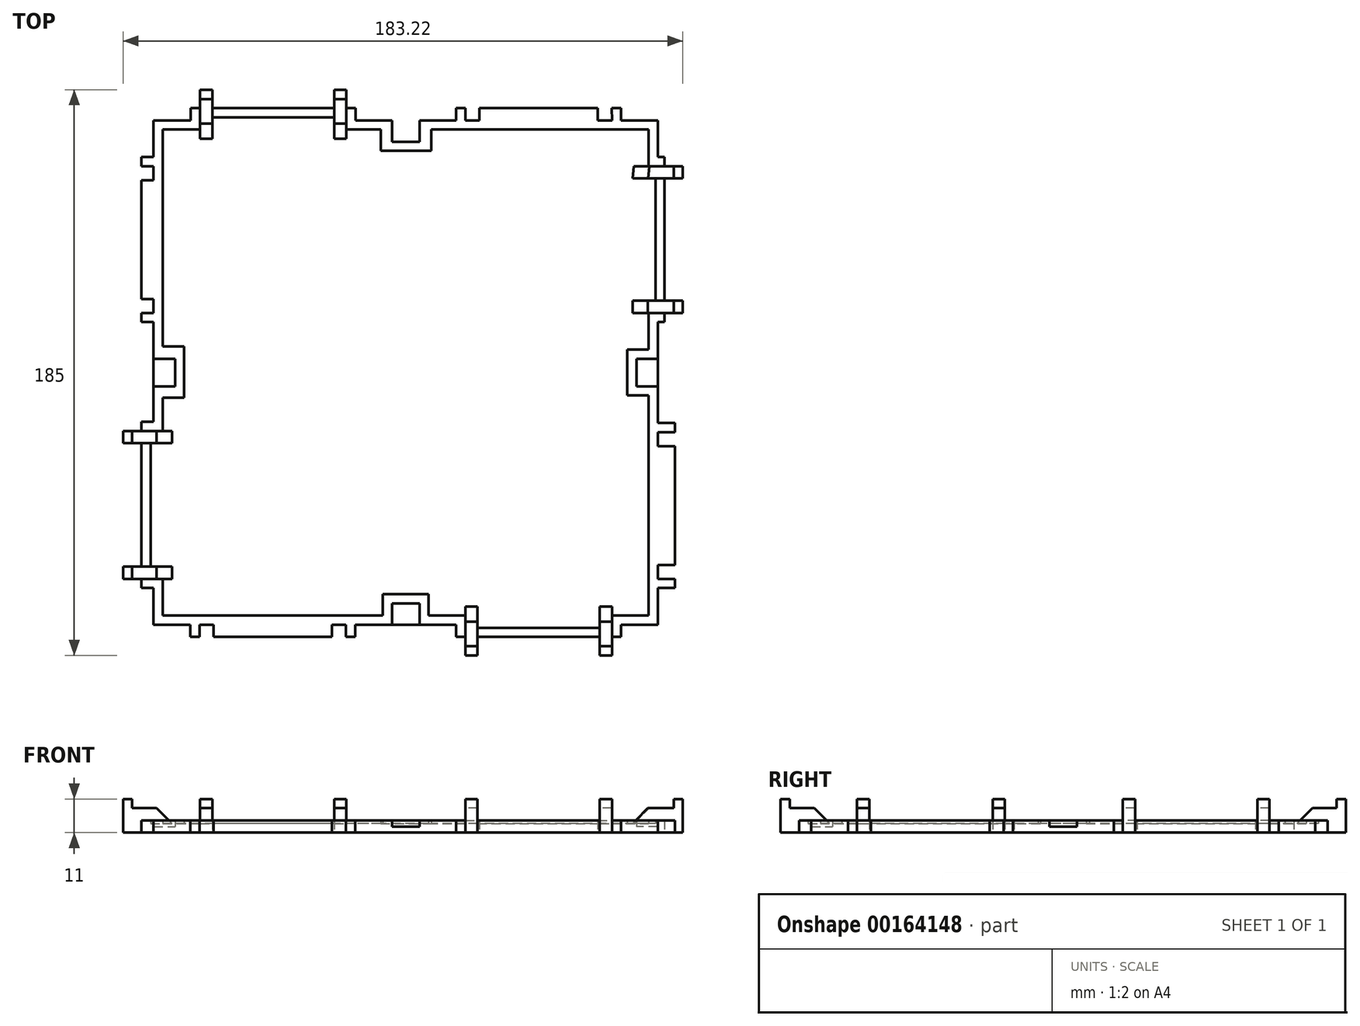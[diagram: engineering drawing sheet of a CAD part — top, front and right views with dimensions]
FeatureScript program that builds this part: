
annotation { "Feature Type Name" : "Feature", "Feature Type Description" : "" }
export const myFeature = defineFeature(function(context is Context, id is Id, definition is map)
    precondition{}
    {
        {
            var Q0;
            Q0=qCreatedBy(makeId("Top.planeOp"),FACE);
            var sketch = newSketch(context, id + "F0", { "sketchPlane" : qUnion([Q0])});
            skLineSegment(sketch, "E0.bottom", {"start": v(-87, 71.22) * mm, "end": v(-74.88, 71.22) * mm});
            skLineSegment(sketch, "E0.top", {"start": v(-87, -93.78) * mm, "end": v(-75, -93.78) * mm});
            skLineSegment(sketch, "E0.left", {"start": v(-87, 71.22) * mm, "end": v(-87, 59.22) * mm});
            skLineSegment(sketch, "E0.right", {"start": v(78, 71.22) * mm, "end": v(78, 59.22) * mm});
            skLineSegment(sketch, "E1", {"start": v(-87, 74.23) * mm, "end": v(-75, 74.23) * mm, "construction": true});
            skLineSegment(sketch, "E2.bottom", {"start": v(-74.88, 75.22) * mm, "end": v(-71.8, 75.22) * mm});
            skLineSegment(sketch, "E2.left", {"start": v(-74.88, 75.22) * mm, "end": v(-74.88, 71.22) * mm});
            skLineSegment(sketch, "E2.right", {"start": v(-20.88, 75.22) * mm, "end": v(-20.88, 71.22) * mm});
            skLineSegment(sketch, "E3", {"start": v(-74.8, 76.18) * mm, "end": v(-71.8, 76.18) * mm, "construction": true});
            skLineSegment(sketch, "E4.bottom", {"start": v(-71.8, 81.22) * mm, "end": v(-67.8, 81.22) * mm});
            skLineSegment(sketch, "E4.left", {"start": v(-71.8, 81.22) * mm, "end": v(-71.8, 75.22) * mm});
            skLineSegment(sketch, "E4.right", {"start": v(-67.8, 81.22) * mm, "end": v(-67.8, 75.22) * mm});
            skLineSegment(sketch, "E5", {"start": v(-20.88, 76.3) * mm, "end": v(-23.88, 76.3) * mm, "construction": true});
            skLineSegment(sketch, "E6.bottom", {"start": v(-27.88, 81.22) * mm, "end": v(-23.88, 81.22) * mm});
            skLineSegment(sketch, "E6.left", {"start": v(-27.88, 81.22) * mm, "end": v(-27.88, 75.22) * mm});
            skLineSegment(sketch, "E6.right", {"start": v(-23.88, 81.22) * mm, "end": v(-23.88, 75.22) * mm});
            skLineSegment(sketch, "E7.bottom", {"start": v(12, 75.22) * mm, "end": v(15, 75.22) * mm});
            skLineSegment(sketch, "E7.top", {"start": v(15, 71.22) * mm, "end": v(19.6, 71.22) * mm});
            skLineSegment(sketch, "E7.left", {"start": v(12, 75.22) * mm, "end": v(12, 71.22) * mm});
            skLineSegment(sketch, "E7.right", {"start": v(66, 75.22) * mm, "end": v(66, 71.22) * mm});
            skLineSegment(sketch, "E8", {"start": v(66, 73.22) * mm, "end": v(63, 73.22) * mm, "construction": true});
            skLineSegment(sketch, "E9", {"start": v(63, 73.22) * mm, "end": v(63, 73.22) * mm, "construction": true});
            skLineSegment(sketch, "E10", {"start": v(15, 75.22) * mm, "end": v(15, 71.22) * mm});
            skLineSegment(sketch, "E11", {"start": v(19.6, 75.22) * mm, "end": v(19.6, 71.22) * mm});
            skLineSegment(sketch, "E12", {"start": v(62.99, 75.22) * mm, "end": v(63, 71.22) * mm});
            skLineSegment(sketch, "E13", {"start": v(58.39, 75.22) * mm, "end": v(58.4, 71.22) * mm});
            skLineSegment(sketch, "E14.bottom", {"start": v(78, 59.22) * mm, "end": v(80.22, 59.22) * mm});
            skLineSegment(sketch, "E14.top", {"start": v(78, 5.22) * mm, "end": v(80.22, 5.22) * mm});
            skLineSegment(sketch, "E14.right", {"start": v(80.22, 59.22) * mm, "end": v(80.22, 56.22) * mm});
            skLineSegment(sketch, "E15.bottom", {"start": v(80.22, 56.22) * mm, "end": v(86.22, 56.22) * mm});
            skLineSegment(sketch, "E15.top", {"start": v(80.22, 52.22) * mm, "end": v(86.22, 52.22) * mm});
            skLineSegment(sketch, "E15.right", {"start": v(86.22, 56.22) * mm, "end": v(86.22, 52.22) * mm});
            skLineSegment(sketch, "E16.bottom", {"start": v(80.22, 12.22) * mm, "end": v(86.22, 12.22) * mm});
            skLineSegment(sketch, "E16.top", {"start": v(80.22, 8.22) * mm, "end": v(86.22, 8.22) * mm});
            skLineSegment(sketch, "E16.right", {"start": v(86.22, 12.22) * mm, "end": v(86.22, 8.22) * mm});
            skLineSegment(sketch, "E17.bottom", {"start": v(78, -27.78) * mm, "end": v(83.62, -27.78) * mm});
            skLineSegment(sketch, "E17.top", {"start": v(78, -81.78) * mm, "end": v(83.62, -81.78) * mm});
            skLineSegment(sketch, "E17.left", {"start": v(78, -30.78) * mm, "end": v(78, -35.38) * mm});
            skLineSegment(sketch, "E17.right", {"start": v(83.62, -27.78) * mm, "end": v(83.62, -30.78) * mm});
            skLineSegment(sketch, "E18.trimOffspring", {"start": v(19.6, 75.22) * mm, "end": v(58.39, 75.22) * mm});
            skLineSegment(sketch, "E19.trimOffspring", {"start": v(62.99, 75.22) * mm, "end": v(66, 75.22) * mm});
            skLineSegment(sketch, "E20", {"start": v(83.62, -78.78) * mm, "end": v(78, -78.78) * mm});
            skLineSegment(sketch, "E21", {"start": v(83.62, -74.18) * mm, "end": v(78, -74.18) * mm});
            skLineSegment(sketch, "E22", {"start": v(83.62, -30.78) * mm, "end": v(78, -30.78) * mm});
            skLineSegment(sketch, "E23", {"start": v(83.62, -35.38) * mm, "end": v(78, -35.38) * mm});
            skLineSegment(sketch, "E24.trimOffspring", {"start": v(83.62, -35.38) * mm, "end": v(83.62, -74.18) * mm});
            skLineSegment(sketch, "E25.trimOffspring", {"start": v(83.62, -78.78) * mm, "end": v(83.62, -81.78) * mm});
            skLineSegment(sketch, "E26.bottom", {"start": v(66, -97.78) * mm, "end": v(63, -97.78) * mm});
            skLineSegment(sketch, "E26.left", {"start": v(66, -97.78) * mm, "end": v(66, -93.78) * mm});
            skLineSegment(sketch, "E26.right", {"start": v(12, -97.78) * mm, "end": v(12, -93.78) * mm});
            skLineSegment(sketch, "E27.top", {"start": v(59, -103.78) * mm, "end": v(63, -103.78) * mm});
            skLineSegment(sketch, "E27.left", {"start": v(59, -97.78) * mm, "end": v(59, -103.78) * mm});
            skLineSegment(sketch, "E27.right", {"start": v(63, -97.78) * mm, "end": v(63, -103.78) * mm});
            skLineSegment(sketch, "E28.top", {"start": v(15, -103.78) * mm, "end": v(19, -103.78) * mm});
            skLineSegment(sketch, "E28.left", {"start": v(15, -97.4) * mm, "end": v(15, -103.78) * mm});
            skLineSegment(sketch, "E28.right", {"start": v(19, -97.78) * mm, "end": v(19, -103.78) * mm});
            skLineSegment(sketch, "E29.trimOffspring", {"start": v(58.4, 73.23) * mm, "end": v(58.39, 73.23) * mm, "construction": true});
            skLineSegment(sketch, "E30.bottom", {"start": v(-72, -93.78) * mm, "end": v(-67.4, -93.78) * mm});
            skLineSegment(sketch, "E30.top", {"start": v(-75, -97.78) * mm, "end": v(-72, -97.78) * mm});
            skLineSegment(sketch, "E30.left", {"start": v(-75, -93.78) * mm, "end": v(-75, -97.78) * mm});
            skLineSegment(sketch, "E30.right", {"start": v(-21, -93.78) * mm, "end": v(-21, -97.78) * mm});
            skLineSegment(sketch, "E31", {"start": v(-72, -97.78) * mm, "end": v(-72, -93.78) * mm});
            skLineSegment(sketch, "E32", {"start": v(-67.4, -97.78) * mm, "end": v(-67.4, -93.78) * mm});
            skLineSegment(sketch, "E33", {"start": v(-24, -93.78) * mm, "end": v(-24, -97.78) * mm});
            skLineSegment(sketch, "E34", {"start": v(-28.6, -93.78) * mm, "end": v(-28.6, -97.78) * mm});
            skLineSegment(sketch, "E35.trimOffspring", {"start": v(-67.4, -97.78) * mm, "end": v(-28.6, -97.78) * mm});
            skLineSegment(sketch, "E36.trimOffspring", {"start": v(-24, -97.78) * mm, "end": v(-21, -97.78) * mm});
            skLineSegment(sketch, "E37.bottom", {"start": v(-91, -27.4) * mm, "end": v(-87, -27.4) * mm});
            skLineSegment(sketch, "E37.top", {"start": v(-91, -81.78) * mm, "end": v(-87, -81.78) * mm});
            skLineSegment(sketch, "E37.left", {"start": v(-91, -27.4) * mm, "end": v(-91, -30.4) * mm});
            skLineSegment(sketch, "E38.bottom", {"start": v(-97, -74.78) * mm, "end": v(-91.24, -74.78) * mm});
            skLineSegment(sketch, "E38.top", {"start": v(-97, -78.78) * mm, "end": v(-91, -78.78) * mm});
            skLineSegment(sketch, "E38.left", {"start": v(-97, -74.78) * mm, "end": v(-97, -78.78) * mm});
            skLineSegment(sketch, "E39.bottom", {"start": v(-97, -30.4) * mm, "end": v(-91, -30.4) * mm});
            skLineSegment(sketch, "E39.top", {"start": v(-97, -34.4) * mm, "end": v(-91, -34.4) * mm});
            skLineSegment(sketch, "E39.left", {"start": v(-97, -30.4) * mm, "end": v(-97, -34.4) * mm});
            skLineSegment(sketch, "E40.bottom", {"start": v(-91, 59.22) * mm, "end": v(-87, 59.22) * mm});
            skLineSegment(sketch, "E40.top", {"start": v(-91, 5.22) * mm, "end": v(-87, 5.22) * mm});
            skLineSegment(sketch, "E40.left", {"start": v(-91, 59.22) * mm, "end": v(-91, 56.22) * mm});
            skLineSegment(sketch, "E40.right", {"start": v(-87, 56.22) * mm, "end": v(-87, 51.62) * mm});
            skLineSegment(sketch, "E41", {"start": v(-91, 56.22) * mm, "end": v(-87, 56.22) * mm});
            skLineSegment(sketch, "E42", {"start": v(-91, 51.62) * mm, "end": v(-87, 51.62) * mm});
            skLineSegment(sketch, "E43", {"start": v(-91, 8.22) * mm, "end": v(-87, 8.22) * mm});
            skLineSegment(sketch, "E44", {"start": v(-91, 12.82) * mm, "end": v(-87, 12.82) * mm});
            skLineSegment(sketch, "E45.trimOffspring", {"start": v(-91, 51.62) * mm, "end": v(-91, 12.82) * mm});
            skLineSegment(sketch, "E46.trimOffspring", {"start": v(-91, 8.22) * mm, "end": v(-91, 5.22) * mm});
            skLineSegment(sketch, "E47", {"start": v(-67.8, 78.22) * mm, "end": v(-71.8, 78.22) * mm});
            skLineSegment(sketch, "E48", {"start": v(-27.88, 78.22) * mm, "end": v(-23.88, 78.22) * mm});
            skLineSegment(sketch, "E49", {"start": v(83.22, 56.22) * mm, "end": v(83.22, 52.22) * mm});
            skLineSegment(sketch, "E50", {"start": v(83.22, 12.22) * mm, "end": v(83.22, 8.22) * mm});
            skLineSegment(sketch, "E51", {"start": v(15, -100.78) * mm, "end": v(19, -100.78) * mm});
            skLineSegment(sketch, "E52", {"start": v(63, -100.78) * mm, "end": v(59, -100.78) * mm});
            skLineSegment(sketch, "E53", {"start": v(-94, -78.78) * mm, "end": v(-94, -74.78) * mm});
            skLineSegment(sketch, "E54", {"start": v(-94, -30.4) * mm, "end": v(-94, -34.4) * mm});
            skLineSegment(sketch, "E55.bottom", {"start": v(-91, -78.78) * mm, "end": v(-81, -78.78) * mm});
            skLineSegment(sketch, "E55.top", {"start": v(-91, -74.78) * mm, "end": v(-81, -74.78) * mm});
            skLineSegment(sketch, "E55.right", {"start": v(-81, -78.78) * mm, "end": v(-81, -74.78) * mm});
            skLineSegment(sketch, "E56.trimOffspring", {"start": v(-87, -81.78) * mm, "end": v(-87, -93.78) * mm});
            skLineSegment(sketch, "E57.bottom", {"start": v(-91, -30.4) * mm, "end": v(-81, -30.4) * mm});
            skLineSegment(sketch, "E57.top", {"start": v(-91, -34.4) * mm, "end": v(-81, -34.4) * mm});
            skLineSegment(sketch, "E57.right", {"start": v(-81, -30.4) * mm, "end": v(-81, -34.4) * mm});
            skLineSegment(sketch, "E58.trimOffspring", {"start": v(66, -93.78) * mm, "end": v(78, -93.78) * mm});
            skLineSegment(sketch, "E59.top", {"start": v(19, -87.78) * mm, "end": v(15, -87.78) * mm});
            skLineSegment(sketch, "E59.left", {"start": v(19, -97.78) * mm, "end": v(19, -87.78) * mm});
            skLineSegment(sketch, "E59.right", {"start": v(15, -97.78) * mm, "end": v(15, -87.78) * mm});
            skLineSegment(sketch, "E60.top", {"start": v(59, -87.78) * mm, "end": v(63, -87.78) * mm});
            skLineSegment(sketch, "E60.left", {"start": v(59, -97.78) * mm, "end": v(59, -87.78) * mm});
            skLineSegment(sketch, "E60.right", {"start": v(63, -97.78) * mm, "end": v(63, -87.78) * mm});
            skLineSegment(sketch, "E61.trimOffspring", {"start": v(59, -97.78) * mm, "end": v(19, -97.78) * mm});
            skLineSegment(sketch, "E62.trimOffspring", {"start": v(15, -97.78) * mm, "end": v(12, -97.78) * mm});
            skLineSegment(sketch, "E63.trimOffspring", {"start": v(-91, -34.4) * mm, "end": v(-91, -74.78) * mm});
            skLineSegment(sketch, "E64.trimOffspring", {"start": v(-91, -78.78) * mm, "end": v(-91, -81.78) * mm});
            skLineSegment(sketch, "E65.trimOffspring", {"start": v(78, 5.22) * mm, "end": v(78, -27.78) * mm});
            skLineSegment(sketch, "E66.bottom", {"start": v(80.22, 56.22) * mm, "end": v(70.22, 56.22) * mm});
            skLineSegment(sketch, "E66.top", {"start": v(80.22, 52.22) * mm, "end": v(69.78, 52.22) * mm});
            skLineSegment(sketch, "E66.right", {"start": v(70.22, 56.22) * mm, "end": v(69.78, 52.22) * mm});
            skLineSegment(sketch, "E67.bottom", {"start": v(80.22, 12.22) * mm, "end": v(69.78, 12.22) * mm});
            skLineSegment(sketch, "E67.top", {"start": v(79.78, 8.22) * mm, "end": v(69.78, 8.22) * mm});
            skLineSegment(sketch, "E67.right", {"start": v(69.78, 12.22) * mm, "end": v(69.78, 8.22) * mm});
            skLineSegment(sketch, "E68.trimOffspring", {"start": v(80.22, 8.22) * mm, "end": v(80.22, 5.22) * mm});
            skLineSegment(sketch, "E69.trimOffspring", {"start": v(80.22, 52.22) * mm, "end": v(80.22, 12.22) * mm});
            skLineSegment(sketch, "E70.trimOffspring", {"start": v(-20.88, 71.22) * mm, "end": v(12, 71.22) * mm});
            skLineSegment(sketch, "E71.top", {"start": v(-71.8, 65.22) * mm, "end": v(-67.8, 65.22) * mm});
            skLineSegment(sketch, "E71.left", {"start": v(-71.8, 75.22) * mm, "end": v(-71.8, 65.22) * mm});
            skLineSegment(sketch, "E71.right", {"start": v(-67.8, 75.22) * mm, "end": v(-67.8, 65.22) * mm});
            skLineSegment(sketch, "E72.top", {"start": v(-27.88, 65.22) * mm, "end": v(-23.88, 65.22) * mm});
            skLineSegment(sketch, "E72.left", {"start": v(-27.88, 75.22) * mm, "end": v(-27.88, 65.22) * mm});
            skLineSegment(sketch, "E72.right", {"start": v(-23.88, 75.22) * mm, "end": v(-23.88, 65.22) * mm});
            skLineSegment(sketch, "E73.trimOffspring", {"start": v(-23.88, 75.22) * mm, "end": v(-20.88, 75.22) * mm});
            skLineSegment(sketch, "E74.trimOffspring", {"start": v(-67.8, 75.22) * mm, "end": v(-27.88, 75.22) * mm});
            skLineSegment(sketch, "E75.bottom", {"start": v(-9, 71.22) * mm, "end": v(0, 71.22) * mm});
            skLineSegment(sketch, "E75.top", {"start": v(-9, 64.22) * mm, "end": v(0, 64.22) * mm});
            skLineSegment(sketch, "E75.left", {"start": v(-9, 71.22) * mm, "end": v(-9, 64.22) * mm});
            skLineSegment(sketch, "E75.right", {"start": v(0, 71.22) * mm, "end": v(0, 64.22) * mm});
            skLineSegment(sketch, "E76.bottom", {"start": v(78, -6.78) * mm, "end": v(71, -6.78) * mm});
            skLineSegment(sketch, "E76.top", {"start": v(78, -15.78) * mm, "end": v(71, -15.78) * mm});
            skLineSegment(sketch, "E76.left", {"start": v(78, -6.78) * mm, "end": v(78, -15.78) * mm});
            skLineSegment(sketch, "E76.right", {"start": v(71, -6.78) * mm, "end": v(71, -15.78) * mm});
            skLineSegment(sketch, "E77.bottom", {"start": v(-9, -93.78) * mm, "end": v(0, -93.78) * mm});
            skLineSegment(sketch, "E77.top", {"start": v(-9, -86.78) * mm, "end": v(0, -86.78) * mm});
            skLineSegment(sketch, "E77.left", {"start": v(-9, -93.78) * mm, "end": v(-9, -86.78) * mm});
            skLineSegment(sketch, "E77.right", {"start": v(0, -93.78) * mm, "end": v(0, -86.78) * mm});
            skLineSegment(sketch, "E78.bottom", {"start": v(-87, -6.78) * mm, "end": v(-80, -6.78) * mm});
            skLineSegment(sketch, "E78.top", {"start": v(-87, -15.78) * mm, "end": v(-80, -15.78) * mm});
            skLineSegment(sketch, "E78.left", {"start": v(-87, -6.78) * mm, "end": v(-87, -15.78) * mm});
            skLineSegment(sketch, "E78.right", {"start": v(-80, -6.78) * mm, "end": v(-80, -15.78) * mm});
            skLineSegment(sketch, "E79", {"start": v(-84, 71.22) * mm, "end": v(-84, 68.22) * mm, "construction": true});
            skLineSegment(sketch, "E80", {"start": v(75, 71.22) * mm, "end": v(75, 68.22) * mm, "construction": true});
            skLineSegment(sketch, "E81", {"start": v(75, -93.78) * mm, "end": v(75, -90.78) * mm, "construction": true});
            skLineSegment(sketch, "E82", {"start": v(-84, -93.78) * mm, "end": v(-84, -90.78) * mm, "construction": true});
            skLineSegment(sketch, "E83", {"start": v(0, -86.78) * mm, "end": v(3, -86.78) * mm, "construction": true});
            skLineSegment(sketch, "E84", {"start": v(0, -83.78) * mm, "end": v(0, -86.78) * mm, "construction": true});
            skLineSegment(sketch, "E85", {"start": v(-9, -86.78) * mm, "end": v(-12, -86.78) * mm, "construction": true});
            skLineSegment(sketch, "E86", {"start": v(-9, -83.78) * mm, "end": v(-9, -86.78) * mm, "construction": true});
            skLineSegment(sketch, "E87", {"start": v(-9, 64.22) * mm, "end": v(-9, 61.22) * mm, "construction": true});
            skLineSegment(sketch, "E88", {"start": v(71, -15.78) * mm, "end": v(71, -18.78) * mm, "construction": true});
            skLineSegment(sketch, "E89", {"start": v(71, -6.78) * mm, "end": v(71, -3.78) * mm, "construction": true});
            skLineSegment(sketch, "E90", {"start": v(71, -6.78) * mm, "end": v(68, -6.78) * mm, "construction": true});
            skLineSegment(sketch, "E91", {"start": v(-80, -6.78) * mm, "end": v(-77, -6.78) * mm, "construction": true});
            skLineSegment(sketch, "E92", {"start": v(-84, 68.22) * mm, "end": v(75, 68.22) * mm, "construction": true});
            skLineSegment(sketch, "E93", {"start": v(75, -90.78) * mm, "end": v(-84, -90.78) * mm, "construction": true});
            skLineSegment(sketch, "E94", {"start": v(-84, -90.78) * mm, "end": v(-84, 68.22) * mm, "construction": true});
            skLineSegment(sketch, "E95", {"start": v(6.55, -83.78) * mm, "end": v(-16.3, -83.78) * mm});
            skLineSegment(sketch, "E96", {"start": v(-12, -90.78) * mm, "end": v(-12, -83.78) * mm});
            skLineSegment(sketch, "E97", {"start": v(3, -90.78) * mm, "end": v(3, -83.78) * mm});
            skLineSegment(sketch, "E98", {"start": v(-12.66, 61.22) * mm, "end": v(3.83, 61.22) * mm});
            skLineSegment(sketch, "E99", {"start": v(-12.66, 61.22) * mm, "end": v(-12.66, 68.22) * mm});
            skLineSegment(sketch, "E100", {"start": v(3.83, 61.22) * mm, "end": v(3.83, 68.22) * mm});
            skLineSegment(sketch, "E101", {"start": v(75, -18.78) * mm, "end": v(68.64, -18.78) * mm});
            skLineSegment(sketch, "E102", {"start": v(75, -3.78) * mm, "end": v(68, -3.78) * mm});
            skLineSegment(sketch, "E103", {"start": v(68, -3.78) * mm, "end": v(68, -18.78) * mm});
            skLineSegment(sketch, "E104", {"start": v(68.64, -18.78) * mm, "end": v(68, -18.78) * mm});
            skLineSegment(sketch, "E105", {"start": v(-77, -2.75) * mm, "end": v(-77, -19.51) * mm});
            skLineSegment(sketch, "E106", {"start": v(-77, -19.51) * mm, "end": v(-84, -19.51) * mm});
            skLineSegment(sketch, "E107", {"start": v(-77, -2.75) * mm, "end": v(-84, -2.75) * mm});
            skLineSegment(sketch, "E108", {"start": v(-84, 68.22) * mm, "end": v(-84, -2.75) * mm});
            skLineSegment(sketch, "E109", {"start": v(-84, -19.51) * mm, "end": v(-84, -30.4) * mm});
            skLineSegment(sketch, "E110", {"start": v(-12, -90.78) * mm, "end": v(-84, -90.78) * mm});
            skLineSegment(sketch, "E111", {"start": v(-84, -78.78) * mm, "end": v(-84, -90.78) * mm});
            skLineSegment(sketch, "E112", {"start": v(3, -90.78) * mm, "end": v(15, -90.78) * mm});
            skLineSegment(sketch, "E113", {"start": v(63, -90.78) * mm, "end": v(75, -90.78) * mm});
            skLineSegment(sketch, "E114", {"start": v(75, -90.78) * mm, "end": v(75, -18.78) * mm});
            skLineSegment(sketch, "E115", {"start": v(75, -3.78) * mm, "end": v(75, 8.22) * mm});
            skLineSegment(sketch, "E116", {"start": v(75, 56.22) * mm, "end": v(75, 68.22) * mm});
            skLineSegment(sketch, "E117", {"start": v(75, 68.22) * mm, "end": v(3.83, 68.22) * mm});
            skLineSegment(sketch, "E118", {"start": v(-12.66, 68.22) * mm, "end": v(-23.88, 68.22) * mm});
            skLineSegment(sketch, "E119.trimOffspring", {"start": v(75, 8.22) * mm, "end": v(75, -90.78) * mm, "construction": true});
            skLineSegment(sketch, "E120", {"start": v(-88, -34.4) * mm, "end": v(-88, -74.78) * mm});
            skLineSegment(sketch, "E121", {"start": v(19, -94.78) * mm, "end": v(59, -94.78) * mm});
            skLineSegment(sketch, "E122", {"start": v(77.22, 12.22) * mm, "end": v(77.22, 52.22) * mm});
            skLineSegment(sketch, "E123.trimOffspring", {"start": v(78, -74.18) * mm, "end": v(78, -78.78) * mm});
            skLineSegment(sketch, "E124.trimOffspring", {"start": v(78, -81.78) * mm, "end": v(78, -93.78) * mm});
            skLineSegment(sketch, "E125.trimOffspring", {"start": v(58.4, 71.22) * mm, "end": v(63, 71.22) * mm});
            skLineSegment(sketch, "E126.trimOffspring", {"start": v(66, 71.22) * mm, "end": v(78, 71.22) * mm});
            skLineSegment(sketch, "E127.trimOffspring", {"start": v(-87, 12.82) * mm, "end": v(-87, 8.22) * mm});
            skLineSegment(sketch, "E128.trimOffspring", {"start": v(-87, 5.22) * mm, "end": v(-87, -27.4) * mm});
            skLineSegment(sketch, "E129.trimOffspring", {"start": v(-21, -93.78) * mm, "end": v(12, -93.78) * mm});
            skLineSegment(sketch, "E130.trimOffspring", {"start": v(-28.6, -93.78) * mm, "end": v(-24, -93.78) * mm});
            skLineSegment(sketch, "E131", {"start": v(-27.88, 72.22) * mm, "end": v(-67.8, 72.22) * mm});
            skLineSegment(sketch, "E132", {"start": v(-84, 68.22) * mm, "end": v(-71.8, 68.22) * mm});
            skLineSegment(sketch, "E133", {"start": v(80.22, 8.22) * mm, "end": v(79.78, 8.22) * mm});
            skLineSegment(sketch, "E134", {"start": v(-91.24, -74.78) * mm, "end": v(-91, -74.78) * mm});
            skSolve(sketch);
        }
        {
            var Q0;
            {var subQ5=sQuery(id+"F0.wireOp",EDGE,"E55.right");Q0=makeQuery(id+"F0.imprint","IMPRINT",FACE,{"disambiguationData":[TD([[makeQuery(id+"F0.imprint","IMPRINT",EDGE,{"derivedFrom":subQ5}),-1.0]])]});}
            extrude(context, id + "F1", {"entities" : qUnion([Q0]), "depth" : 3 * mm});
        }
        {
            var Q0;
            Q0=makeQuery(id+"F0.imprint","IMPRINT",FACE,{"disambiguationData":[TD([[makeQuery(id+"F0.imprint","IMPRINT",EDGE,{"derivedFrom":sQuery(id+"F0.wireOp",EDGE,"E0.bottom")}),-1.0]])]});
            var Q1;
            {var subQ0=sQuery(id+"F0.wireOp",EDGE,"E74.trimOffspring");Q1=makeQuery(id+"F0.imprint","IMPRINT",FACE,{"disambiguationData":[TD([[makeQuery(id+"F0.imprint","IMPRINT",EDGE,{"derivedFrom":subQ0}),-1.0]])]});}
            var Q2;
            Q2=makeQuery(id+"F0.imprint","IMPRINT",FACE,{"disambiguationData":[TD([[makeQuery(id+"F0.imprint","IMPRINT",EDGE,{"derivedFrom":sQuery(id+"F0.wireOp",EDGE,"E0.right")}),-1.0]])]});
            var Q3;
            {var subQ0=sQuery(id+"F0.wireOp",EDGE,"E69.trimOffspring");Q3=makeQuery(id+"F0.imprint","IMPRINT",FACE,{"disambiguationData":[TD([[makeQuery(id+"F0.imprint","IMPRINT",EDGE,{"derivedFrom":subQ0}),-1.0]])]});}
            var Q4;
            {var subQ11=sQuery(id+"F0.wireOp",EDGE,"E14.top");Q4=makeQuery(id+"F0.imprint","IMPRINT",FACE,{"disambiguationData":[TD([[makeQuery(id+"F0.imprint","IMPRINT",EDGE,{"derivedFrom":subQ11}),1.0]])]});}
            var Q5;
            {var subQ0=sQuery(id+"F0.wireOp",EDGE,"E61.trimOffspring");Q5=makeQuery(id+"F0.imprint","IMPRINT",FACE,{"disambiguationData":[TD([[makeQuery(id+"F0.imprint","IMPRINT",EDGE,{"derivedFrom":subQ0}),-1.0]])]});}
            var Q6;
            Q6=makeQuery(id+"F0.imprint","IMPRINT",FACE,{"disambiguationData":[TD([[makeQuery(id+"F0.imprint","IMPRINT",EDGE,{"derivedFrom":sQuery(id+"F0.wireOp",EDGE,"E0.top")}),1.0]])]});
            var Q7;
            {var subQ0=sQuery(id+"F0.wireOp",EDGE,"E63.trimOffspring");Q7=makeQuery(id+"F0.imprint","IMPRINT",FACE,{"disambiguationData":[TD([[makeQuery(id+"F0.imprint","IMPRINT",EDGE,{"derivedFrom":subQ0}),1.0]])]});}
            extrude(context, id + "F2", {"entities" : qUnion([Q0, Q1, Q2, Q3, Q4, Q5, Q6, Q7]), "operationType" : NewBodyOperationType.ADD, "depth" : 4 * mm});
        }
        {
            var Q0;
            {var subQ0=sQuery(id+"F0.wireOp",EDGE,"E78.bottom");Q0=makeQuery(id+"F0.imprint","IMPRINT",FACE,{"disambiguationData":[TD([[makeQuery(id+"F0.imprint","IMPRINT",EDGE,{"derivedFrom":subQ0}),-1.0]])]});}
            var Q1;
            Q1=makeQuery(id+"F0.imprint","IMPRINT",FACE,{"disambiguationData":[TD([[makeQuery(id+"F0.imprint","IMPRINT",EDGE,{"derivedFrom":sQuery(id+"F0.wireOp",EDGE,"E75.bottom")}),-1.0]])]});
            var Q2;
            Q2=makeQuery(id+"F0.imprint","IMPRINT",FACE,{"disambiguationData":[TD([[makeQuery(id+"F0.imprint","IMPRINT",EDGE,{"derivedFrom":sQuery(id+"F0.wireOp",EDGE,"E76.bottom")}),1.0]])]});
            var Q3;
            Q3=makeQuery(id+"F0.imprint","IMPRINT",FACE,{"disambiguationData":[TD([[makeQuery(id+"F0.imprint","IMPRINT",EDGE,{"derivedFrom":sQuery(id+"F0.wireOp",EDGE,"E77.top")}),-1.0]])]});
            extrude(context, id + "F3", {"entities" : qUnion([Q0, Q1, Q2, Q3]), "operationType" : NewBodyOperationType.ADD, "depth" : 2 * mm});
        }
        {
            var Q0;
            {var subQ0=sQuery(id+"F0.wireOp",EDGE,"E47");Q0=makeQuery(id+"F0.imprint","IMPRINT",FACE,{"disambiguationData":[TD([[makeQuery(id+"F0.imprint","IMPRINT",EDGE,{"derivedFrom":subQ0}),1.0]])]});}
            var Q1;
            {var subQ0=sQuery(id+"F0.wireOp",EDGE,"E48");Q1=makeQuery(id+"F0.imprint","IMPRINT",FACE,{"disambiguationData":[TD([[makeQuery(id+"F0.imprint","IMPRINT",EDGE,{"derivedFrom":subQ0}),-1.0]])]});}
            var Q2;
            {var subQ4=sQuery(id+"F0.wireOp",EDGE,"E49");Q2=makeQuery(id+"F0.imprint","IMPRINT",FACE,{"disambiguationData":[TD([[makeQuery(id+"F0.imprint","IMPRINT",EDGE,{"derivedFrom":subQ4}),-1.0]])]});}
            var Q3;
            {var subQ0=sQuery(id+"F0.wireOp",EDGE,"E50");Q3=makeQuery(id+"F0.imprint","IMPRINT",FACE,{"disambiguationData":[TD([[makeQuery(id+"F0.imprint","IMPRINT",EDGE,{"derivedFrom":subQ0}),-1.0]])]});}
            var Q4;
            {var subQ0=sQuery(id+"F0.wireOp",EDGE,"E52");Q4=makeQuery(id+"F0.imprint","IMPRINT",FACE,{"disambiguationData":[TD([[makeQuery(id+"F0.imprint","IMPRINT",EDGE,{"derivedFrom":subQ0}),-1.0]])]});}
            var Q5;
            {var subQ1=sQuery(id+"F0.wireOp",EDGE,"E51");Q5=makeQuery(id+"F0.imprint","IMPRINT",FACE,{"disambiguationData":[TD([[makeQuery(id+"F0.imprint","IMPRINT",EDGE,{"derivedFrom":subQ1}),1.0]])]});}
            var Q6;
            {var subQ4=sQuery(id+"F0.wireOp",EDGE,"E54");Q6=makeQuery(id+"F0.imprint","IMPRINT",FACE,{"disambiguationData":[TD([[makeQuery(id+"F0.imprint","IMPRINT",EDGE,{"derivedFrom":subQ4}),1.0]])]});}
            var Q7;
            {var subQ4=sQuery(id+"F0.wireOp",EDGE,"E53");Q7=makeQuery(id+"F0.imprint","IMPRINT",FACE,{"disambiguationData":[TD([[makeQuery(id+"F0.imprint","IMPRINT",EDGE,{"derivedFrom":subQ4}),-1.0]])]});}
            extrude(context, id + "F4", {"entities" : qUnion([Q0, Q1, Q2, Q3, Q4, Q5, Q6, Q7]), "operationType" : NewBodyOperationType.ADD, "depth" : 8 * mm});
        }
        {
            var Q0;
            {var subQ0=sQuery(id+"F0.wireOp",EDGE,"E39.left");Q0=makeQuery(id+"F0.imprint","IMPRINT",FACE,{"disambiguationData":[TD([[makeQuery(id+"F0.imprint","IMPRINT",EDGE,{"derivedFrom":subQ0}),1.0]])]});}
            var Q1;
            {var subQ0=sQuery(id+"F0.wireOp",EDGE,"E38.left");Q1=makeQuery(id+"F0.imprint","IMPRINT",FACE,{"disambiguationData":[TD([[makeQuery(id+"F0.imprint","IMPRINT",EDGE,{"derivedFrom":subQ0}),1.0]])]});}
            var Q2;
            {var subQ0=sQuery(id+"F0.wireOp",EDGE,"E28.top");Q2=makeQuery(id+"F0.imprint","IMPRINT",FACE,{"disambiguationData":[TD([[makeQuery(id+"F0.imprint","IMPRINT",EDGE,{"derivedFrom":subQ0}),1.0]])]});}
            var Q3;
            {var subQ0=sQuery(id+"F0.wireOp",EDGE,"E27.top");Q3=makeQuery(id+"F0.imprint","IMPRINT",FACE,{"disambiguationData":[TD([[makeQuery(id+"F0.imprint","IMPRINT",EDGE,{"derivedFrom":subQ0}),1.0]])]});}
            var Q4;
            {var subQ0=sQuery(id+"F0.wireOp",EDGE,"E16.right");Q4=makeQuery(id+"F0.imprint","IMPRINT",FACE,{"disambiguationData":[TD([[makeQuery(id+"F0.imprint","IMPRINT",EDGE,{"derivedFrom":subQ0}),-1.0]])]});}
            var Q5;
            {var subQ0=sQuery(id+"F0.wireOp",EDGE,"E15.right");Q5=makeQuery(id+"F0.imprint","IMPRINT",FACE,{"disambiguationData":[TD([[makeQuery(id+"F0.imprint","IMPRINT",EDGE,{"derivedFrom":subQ0}),-1.0]])]});}
            var Q6;
            {var subQ0=sQuery(id+"F0.wireOp",EDGE,"E6.bottom");Q6=makeQuery(id+"F0.imprint","IMPRINT",FACE,{"disambiguationData":[TD([[makeQuery(id+"F0.imprint","IMPRINT",EDGE,{"derivedFrom":subQ0}),-1.0]])]});}
            var Q7;
            {var subQ0=sQuery(id+"F0.wireOp",EDGE,"E4.bottom");Q7=makeQuery(id+"F0.imprint","IMPRINT",FACE,{"disambiguationData":[TD([[makeQuery(id+"F0.imprint","IMPRINT",EDGE,{"derivedFrom":subQ0}),-1.0]])]});}
            extrude(context, id + "F5", {"entities" : qUnion([Q0, Q1, Q2, Q3, Q4, Q5, Q6, Q7]), "operationType" : NewBodyOperationType.ADD, "depth" : 11 * mm});
        }
        {
            var Q0;
            Q0=makeQuery(id+"F4.opExtrude","CAP_EDGE",EDGE,{"disambiguationData":[OSD([sQuery(id+"F0.wireOp",EDGE,"E71.top")])],"isStart":false});
            var Q1;
            Q1=makeQuery(id+"F4.opExtrude","CAP_EDGE",EDGE,{"disambiguationData":[OSD([sQuery(id+"F0.wireOp",EDGE,"E72.top")])],"isStart":false});
            var Q2;
            Q2=makeQuery(id+"F4.opExtrude","CAP_EDGE",EDGE,{"disambiguationData":[OSD([sQuery(id+"F0.wireOp",EDGE,"E66.right")])],"isStart":false});
            var Q3;
            Q3=makeQuery(id+"F4.opExtrude","CAP_EDGE",EDGE,{"disambiguationData":[OSD([sQuery(id+"F0.wireOp",EDGE,"E67.right")])],"isStart":false});
            var Q4;
            Q4=makeQuery(id+"F4.opExtrude","CAP_EDGE",EDGE,{"disambiguationData":[OSD([sQuery(id+"F0.wireOp",EDGE,"E55.right")])],"isStart":false});
            var Q5;
            Q5=makeQuery(id+"F4.opExtrude","CAP_EDGE",EDGE,{"disambiguationData":[OSD([sQuery(id+"F0.wireOp",EDGE,"E57.right")])],"isStart":false});
            var Q6;
            Q6=makeQuery(id+"F4.opExtrude","CAP_EDGE",EDGE,{"disambiguationData":[OSD([sQuery(id+"F0.wireOp",EDGE,"E60.top")])],"isStart":false});
            var Q7;
            Q7=makeQuery(id+"F4.opExtrude","CAP_EDGE",EDGE,{"disambiguationData":[OSD([sQuery(id+"F0.wireOp",EDGE,"E59.top")])],"isStart":false});
            chamfer(context, id + "F6", {"entities" : qUnion([Q0, Q1, Q2, Q3, Q4, Q5, Q6, Q7]), "width" : 5 * mm, "tangentPropagation" : true});
        }
    });
